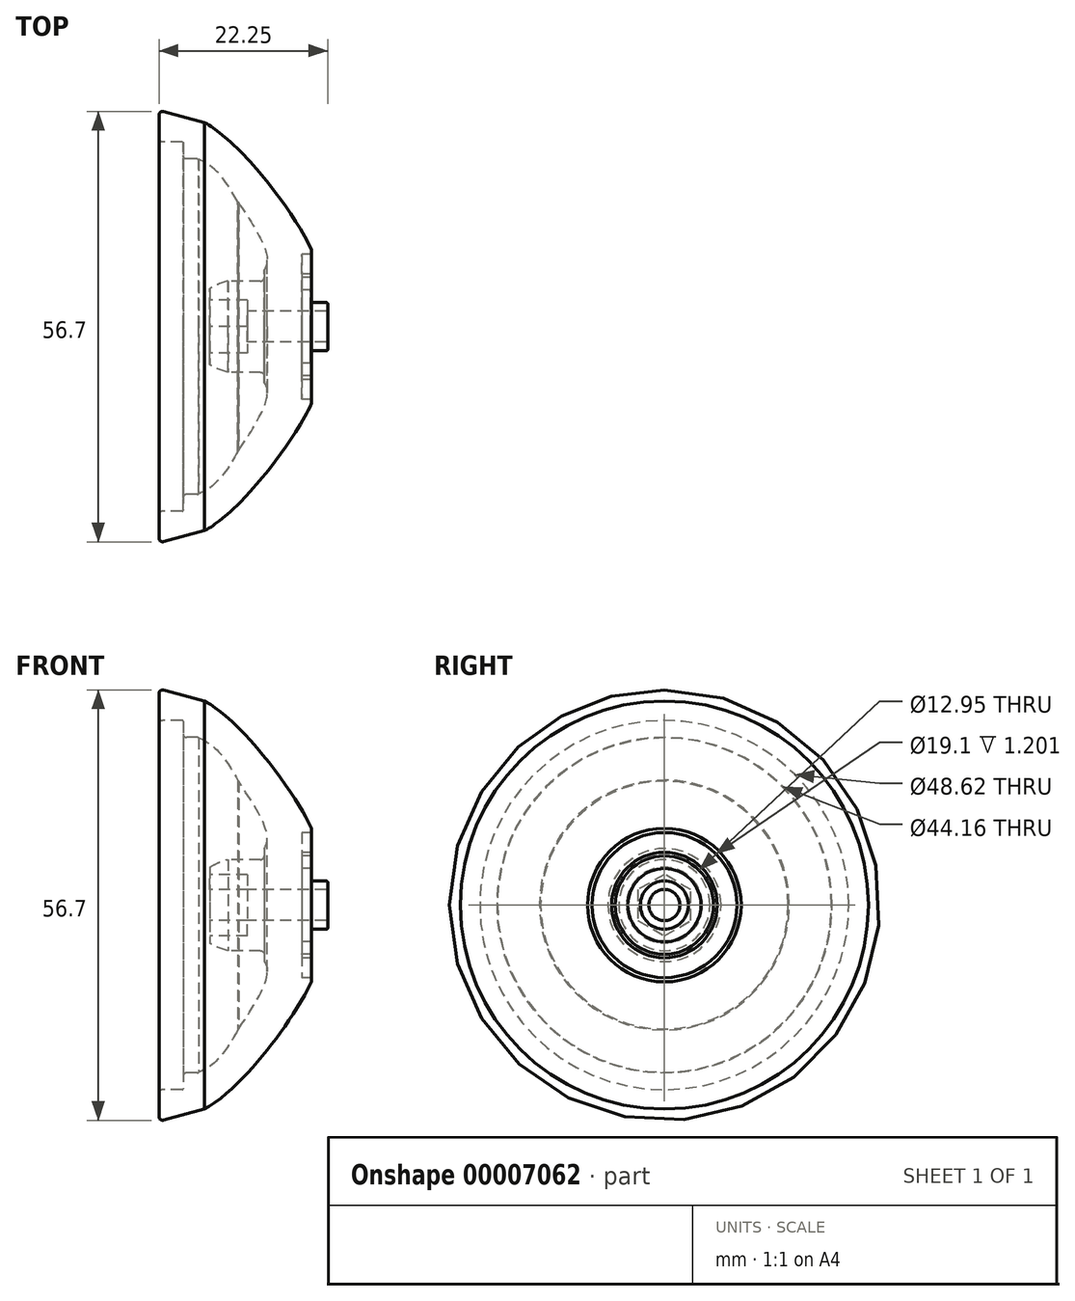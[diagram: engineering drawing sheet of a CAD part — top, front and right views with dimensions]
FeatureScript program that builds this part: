
annotation { "Feature Type Name" : "Feature", "Feature Type Description" : "" }
export const myFeature = defineFeature(function(context is Context, id is Id, definition is map)
    precondition{}
    {
        {
            var Q0;
            Q0=qCreatedBy(makeId("Front.planeOp"),FACE);
            var sketch = newSketch(context, id + "F0", { "sketchPlane" : qUnion([Q0])});
            skLineSegment(sketch, "E0", {"start": v(-27.14, 28.5) * mm, "end": v(36.68, 28.5) * mm, "construction": true});
            skLineSegment(sketch, "E1", {"start": v(20, 42.96) * mm, "end": v(20, -13.53) * mm, "construction": true});
            skLineSegment(sketch, "E2.bottom", {"start": v(22.05, 3.18) * mm, "end": v(20.1, 3.18) * mm});
            skLineSegment(sketch, "E2.left", {"start": v(22.25, 2.98) * mm, "end": v(22.25, 2.25) * mm});
            skLineSegment(sketch, "E3", {"start": v(20, 3.28) * mm, "end": v(20, 4.82) * mm});
            skLineSegment(sketch, "E4", {"start": v(20, 4.82) * mm, "end": v(18.9, 4.82) * mm});
            skLineSegment(sketch, "E5", {"start": v(18.8, 4.92) * mm, "end": v(18.8, 6.38) * mm});
            skLineSegment(sketch, "E6", {"start": v(18.9, 6.48) * mm, "end": v(20, 6.48) * mm});
            skLineSegment(sketch, "E7", {"start": v(20, 6.95) * mm, "end": v(18.8, 6.95) * mm});
            skLineSegment(sketch, "E8", {"start": v(18.8, 6.95) * mm, "end": v(18.8, 9.55) * mm});
            skLineSegment(sketch, "E9", {"start": v(18.8, 9.55) * mm, "end": v(20, 9.55) * mm});
            skLineSegment(sketch, "E10", {"start": v(6, 26.88) * mm, "end": v(0.63, 28.33) * mm});
            skLineSegment(sketch, "E11", {"start": v(0, 27.85) * mm, "end": v(0, 24.8) * mm});
            skLineSegment(sketch, "E12", {"start": v(0.5, 24.3) * mm, "end": v(3.08, 24.3) * mm});
            skLineSegment(sketch, "E13", {"start": v(3.18, 24.2) * mm, "end": v(3.18, 22.58) * mm});
            skLineSegment(sketch, "E14", {"start": v(10.46, 16.37) * mm, "end": v(13.8, 10.48) * mm});
            skLineSegment(sketch, "E15", {"start": v(13.88, 10.23) * mm, "end": v(13.88, 6.5) * mm});
            skLineSegment(sketch, "E16", {"start": v(13.38, 6) * mm, "end": v(7.68, 6) * mm});
            skLineSegment(sketch, "E17", {"start": v(6.68, 5) * mm, "end": v(6.68, 2.25) * mm});
            skLineSegment(sketch, "E18", {"start": v(6.68, 0) * mm, "end": v(6.68, 0) * mm});
            skLineSegment(sketch, "E19", {"start": v(6.68, 0) * mm, "end": v(22.25, 0) * mm});
            skLineSegment(sketch, "E20.top", {"start": v(20.1, 6.48) * mm, "end": v(20.1, 6.48) * mm});
            skLineSegment(sketch, "E20.left", {"start": v(20.1, 6.85) * mm, "end": v(20.1, 6.58) * mm});
            skLineSegment(sketch, "E21.right", {"start": v(20.1, 9.65) * mm, "end": v(20.1, 10) * mm});
            skLineSegment(sketch, "E22", {"start": v(3.68, 22.08) * mm, "end": v(5.03, 22.08) * mm});
            skPoint(sketch, "E23.visualSharp", {"position": v(0, 28.5) * mm});
            skArc(sketch, "E23.filletArc", {"start": v(0.63, 28.33) * mm, "mid": v(0.2, 28.24) * mm, "end": v(0, 27.85) * mm});
            skPoint(sketch, "E24.visualSharp", {"position": v(20.1, 10.09) * mm});
            skArc(sketch, "E24.filletArc", {"start": v(20.1, 10) * mm, "mid": v(20.1, 10.06) * mm, "end": v(20.1, 10.12) * mm});
            skPoint(sketch, "E25.visualSharp", {"position": v(6.68, 6) * mm});
            skArc(sketch, "E25.filletArc", {"start": v(7.68, 6) * mm, "mid": v(6.97, 5.7) * mm, "end": v(6.68, 5) * mm});
            skPoint(sketch, "E26.visualSharp", {"position": v(20.1, 9.55) * mm});
            skArc(sketch, "E26.filletArc", {"start": v(20, 9.55) * mm, "mid": v(20.07, 9.58) * mm, "end": v(20.1, 9.65) * mm});
            skPoint(sketch, "E27.visualSharp", {"position": v(20.1, 6.95) * mm});
            skArc(sketch, "E27.filletArc", {"start": v(20.1, 6.85) * mm, "mid": v(20.07, 6.92) * mm, "end": v(20, 6.95) * mm});
            skPoint(sketch, "E28.visualSharp", {"position": v(20.1, 6.48) * mm});
            skArc(sketch, "E28.filletArc", {"start": v(20, 6.48) * mm, "mid": v(20.07, 6.5) * mm, "end": v(20.1, 6.58) * mm});
            skPoint(sketch, "E29.visualSharp", {"position": v(18.8, 6.48) * mm});
            skArc(sketch, "E29.filletArc", {"start": v(18.9, 6.48) * mm, "mid": v(18.83, 6.45) * mm, "end": v(18.8, 6.38) * mm});
            skPoint(sketch, "E30.visualSharp", {"position": v(18.8, 4.82) * mm});
            skArc(sketch, "E30.filletArc", {"start": v(18.8, 4.92) * mm, "mid": v(18.83, 4.85) * mm, "end": v(18.9, 4.82) * mm});
            skPoint(sketch, "E31.visualSharp", {"position": v(20, 3.18) * mm});
            skArc(sketch, "E31.filletArc", {"start": v(20, 3.28) * mm, "mid": v(20.03, 3.2) * mm, "end": v(20.1, 3.18) * mm});
            skPoint(sketch, "E32.visualSharp", {"position": v(22.25, 3.18) * mm});
            skArc(sketch, "E32.filletArc", {"start": v(22.25, 2.98) * mm, "mid": v(22.2, 3.12) * mm, "end": v(22.05, 3.18) * mm});
            skLineSegment(sketch, "E33", {"start": v(22.05, 2.05) * mm, "end": v(6.88, 2.05) * mm});
            skPoint(sketch, "E34.visualSharp", {"position": v(0, 24.3) * mm});
            skArc(sketch, "E34.filletArc", {"start": v(0, 24.8) * mm, "mid": v(0.15, 24.46) * mm, "end": v(0.5, 24.3) * mm});
            skPoint(sketch, "E35.visualSharp", {"position": v(3.18, 22.08) * mm});
            skArc(sketch, "E35.filletArc", {"start": v(3.18, 22.58) * mm, "mid": v(3.32, 22.23) * mm, "end": v(3.68, 22.08) * mm});
            skPoint(sketch, "E36.visualSharp", {"position": v(5.15, 22.08) * mm});
            skArc(sketch, "E36.filletArc", {"start": v(5.27, 22.02) * mm, "mid": v(5.15, 22.06) * mm, "end": v(5.03, 22.08) * mm});
            skPoint(sketch, "E37.visualSharp", {"position": v(10.43, 16.42) * mm});
            skArc(sketch, "E37.filletArc", {"start": v(10.46, 16.37) * mm, "mid": v(10.43, 16.41) * mm, "end": v(10.4, 16.45) * mm});
            skPoint(sketch, "E38.visualSharp", {"position": v(22.25, 2.05) * mm});
            skArc(sketch, "E38.filletArc", {"start": v(22.05, 2.05) * mm, "mid": v(22.2, 2.1) * mm, "end": v(22.25, 2.25) * mm});
            skPoint(sketch, "E39.visualSharp", {"position": v(6.68, 2.05) * mm});
            skArc(sketch, "E39.filletArc", {"start": v(6.68, 2.25) * mm, "mid": v(6.74, 2.1) * mm, "end": v(6.88, 2.05) * mm});
            skPoint(sketch, "E40.visualSharp", {"position": v(13.88, 10.37) * mm});
            skArc(sketch, "E40.filletArc", {"start": v(13.88, 10.23) * mm, "mid": v(13.86, 10.36) * mm, "end": v(13.8, 10.48) * mm});
            skPoint(sketch, "E41.visualSharp", {"position": v(13.88, 6) * mm});
            skArc(sketch, "E41.filletArc", {"start": v(13.38, 6) * mm, "mid": v(13.73, 6.15) * mm, "end": v(13.88, 6.5) * mm});
            skPoint(sketch, "E42.visualSharp", {"position": v(3.18, 24.3) * mm});
            skArc(sketch, "E42.filletArc", {"start": v(3.18, 24.2) * mm, "mid": v(3.15, 24.28) * mm, "end": v(3.08, 24.3) * mm});
            skFitSpline(sketch, "E43", {"points": [v(6, 26.88) * mm, v(10.06, 23.76) * mm, v(17.72, 14.32) * mm, v(20.1, 10.12) * mm], "startDerivative": vector(6.05, -2.38) * mm, "endDerivative": vector(3.01, -7.52) * mm});
            skFitSpline(sketch, "E44", {"points": [v(5.27, 22.02) * mm, v(10.4, 16.45) * mm], "startDerivative": vector(6.25, -2.6) * mm, "endDerivative": vector(5.37, -9.59) * mm});
            skFitSpline(sketch, "E45", {"points": [v(6.68, 5) * mm, v(9.1, 6) * mm, v(12.28, 6.4) * mm, v(14.27, 8.4) * mm, v(10.4, 16.45) * mm], "startDerivative": vector(11.42, 6.2) * mm, "endDerivative": vector(-16.7, 25.05) * mm});
            skSolve(sketch);
        }
        {
            var Q0;
            Q0=makeQuery(id+"F0.imprint","IMPRINT",FACE,{"disambiguationData":[TD([[makeQuery(id+"F0.imprint","IMPRINT",EDGE,{"derivedFrom":sQuery(id+"F0.wireOp",EDGE,"E2.bottom")}),1.0]])]});
            var Q1;
            Q1=sQuery(id+"F0.wireOp",EDGE,"E19");
            revolve(context, id + "F1", {"entities" : qUnion([Q0]), "axis" : qUnion([Q1]), "revolveType" : RevolveType.FULL});
        }
        {
            var Q0;
            Q0=makeQuery(id+"F1.opRevolve","SWEPT_FACE",FACE,{"disambiguationData":[OSD([sQuery(id+"F0.wireOp",EDGE,"E17")])]});
            var sketch = newSketch(context, id + "F2", { "sketchPlane" : qUnion([Q0])});
            skCircle(sketch, "E46.cCircle", {"center": v(0, 0) * mm, "radius": 3.5 * mm, "construction": true});
            skLineSegment(sketch, "E46.0", {"start": v(3.5, 2.02) * mm, "end": v(3.5, -2.02) * mm});
            skLineSegment(sketch, "E46.1", {"start": v(3.5, -2.02) * mm, "end": v(0, -4.04) * mm});
            skLineSegment(sketch, "E46.2", {"start": v(0, -4.04) * mm, "end": v(-3.5, -2.02) * mm});
            skLineSegment(sketch, "E46.3", {"start": v(-3.5, -2.02) * mm, "end": v(-3.5, 2.02) * mm});
            skLineSegment(sketch, "E46.4", {"start": v(-3.5, 2.02) * mm, "end": v(0, 4.04) * mm});
            skLineSegment(sketch, "E46.5", {"start": v(0, 4.04) * mm, "end": v(3.5, 2.02) * mm});
            skPoint(sketch, "E46.0.midPoint", {"position": v(3.5, 0) * mm});
            skSolve(sketch);
        }
        {
            var Q0;
            Q0=qSketchRegion(id+"F2",true);
            extrude(context, id + "F3", {"entities" : qUnion([Q0]), "operationType" : NewBodyOperationType.REMOVE, "oppositeDirection" : true, "depth" : 5 * mm});
        }
    });
